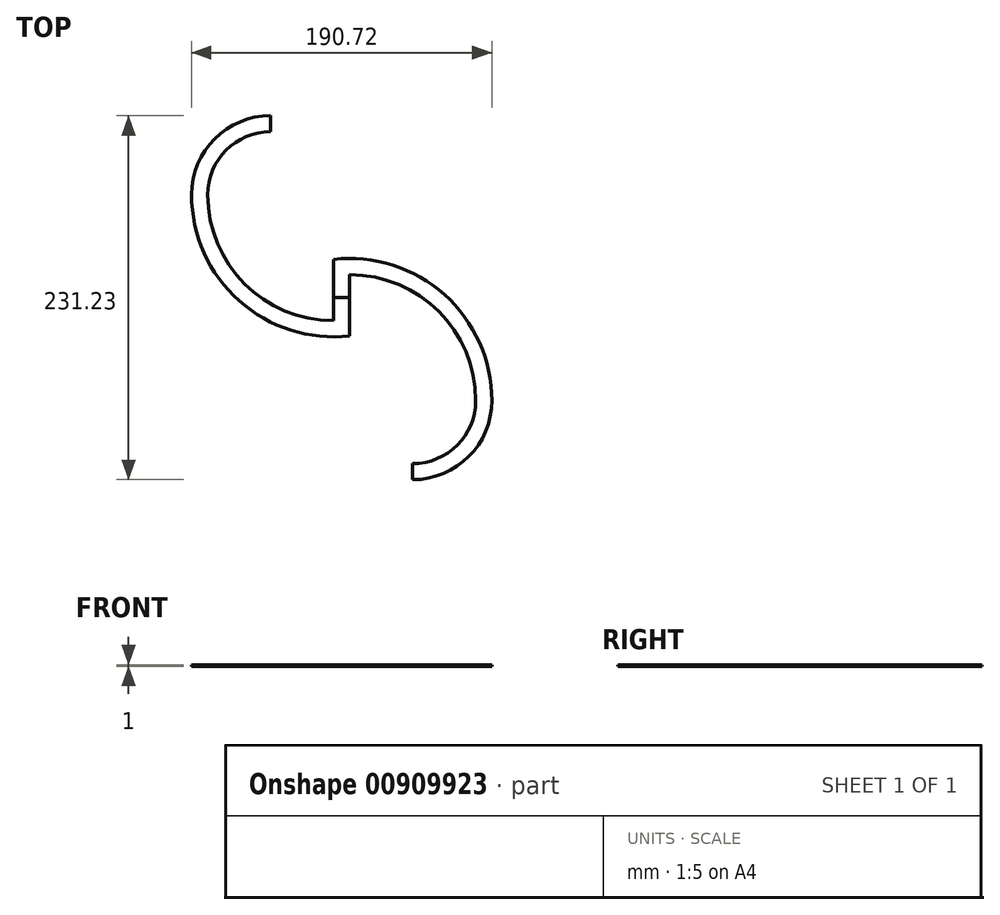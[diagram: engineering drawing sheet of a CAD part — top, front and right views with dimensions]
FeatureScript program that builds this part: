
annotation { "Feature Type Name" : "Feature", "Feature Type Description" : "" }
export const myFeature = defineFeature(function(context is Context, id is Id, definition is map)
    precondition{}
    {
        {
            var Q0;
            Q0=qCreatedBy(makeId("Top.planeOp"),FACE);
            var sketch = newSketch(context, id + "F0", { "sketchPlane" : qUnion([Q0])});
            skArc(sketch, "E0", {"start": v(80, 0) * mm, "mid": v(56.57, 56.57) * mm, "end": v(0, 80) * mm});
            skArc(sketch, "E1", {"start": v(80, 0) * mm, "mid": v(68.28, -28.28) * mm, "end": v(40, -40) * mm});
            skLineSegment(sketch, "E2", {"start": v(0, 80) * mm, "end": v(0, 65.37) * mm});
            skLineSegment(sketch, "E3.0", {"start": v(-10.24, 89.66) * mm, "end": v(-10.24, 65.37) * mm});
            skArc(sketch, "E3.1", {"start": v(90.24, 0) * mm, "mid": v(60.08, 67.33) * mm, "end": v(-10.24, 89.66) * mm});
            skArc(sketch, "E3.2", {"start": v(90.24, 0) * mm, "mid": v(75.53, -35.53) * mm, "end": v(40, -50.24) * mm});
            skLineSegment(sketch, "E4", {"start": v(-10.24, 65.37) * mm, "end": v(0, 65.37) * mm});
            skLineSegment(sketch, "E5", {"start": v(40, -40) * mm, "end": v(40, -50.24) * mm});
            skSolve(sketch);
        }
        {
            var Q0;
            Q0=makeQuery(id+"F0.imprint","IMPRINT",FACE,{"disambiguationData":[TD([[makeQuery(id+"F0.imprint","IMPRINT",EDGE,{"derivedFrom":sQuery(id+"F0.wireOp",EDGE,"E0")}),-1.0]])]});
            extrude(context, id + "F1", {"entities" : qUnion([Q0]), "depth" : 1 * mm, "offsetDistance" : 25 * mm});
        }
        {
            var Q0;
            Q0=makeQuery(id+"F1.opExtrude","SWEPT_BODY",BODY,{"disambiguationData":[OSD([sQuery(id+"F0.wireOp",EDGE,"E0"),sQuery(id+"F0.wireOp",EDGE,"E1"),sQuery(id+"F0.wireOp",EDGE,"E2"),sQuery(id+"F0.wireOp",EDGE,"E3.0"),sQuery(id+"F0.wireOp",EDGE,"E3.1"),sQuery(id+"F0.wireOp",EDGE,"E3.2"),sQuery(id+"F0.wireOp",EDGE,"E4"),sQuery(id+"F0.wireOp",EDGE,"E5")])]});
            var Q1;
            Q1=makeQuery(id+"F1.opExtrude","SWEPT_EDGE",EDGE,{"disambiguationData":[OSD([sQuery(id+"F0.wireOp",EDGE,"E3.0"),sQuery(id+"F0.wireOp",EDGE,"E4")])]});
            transform(context, id + "F2", {"entities" : qUnion([Q0]), "transformType" : TransformType.ROTATION, "transformAxis" : qUnion([Q1]), "angle" : 180 * degree, "makeCopy" : true});
        }
        {
            var Q0;
            Q0=makeQuery(id+"F2.opPattern","COPY",BODY,{"derivedFrom":makeQuery(id+"F1.opExtrude","SWEPT_BODY",BODY,{"disambiguationData":[OSD([sQuery(id+"F0.wireOp",EDGE,"E0"),sQuery(id+"F0.wireOp",EDGE,"E1"),sQuery(id+"F0.wireOp",EDGE,"E2"),sQuery(id+"F0.wireOp",EDGE,"E3.0"),sQuery(id+"F0.wireOp",EDGE,"E3.1"),sQuery(id+"F0.wireOp",EDGE,"E3.2"),sQuery(id+"F0.wireOp",EDGE,"E4"),sQuery(id+"F0.wireOp",EDGE,"E5")])]}),"instanceName":"1"});
            var Q1;
            Q1=makeQuery(id+"F1.opExtrude","CAP_EDGE",EDGE,{"disambiguationData":[OSD([sQuery(id+"F0.wireOp",EDGE,"E4")])],"isStart":false});
            transform(context, id + "F3", {"entities" : qUnion([Q0]), "transformType" : TransformType.TRANSLATION_ENTITY, "oppositeDirectionEntity" : false, "transformLine" : qUnion([Q1]), "makeCopy" : false});
        }
    });
